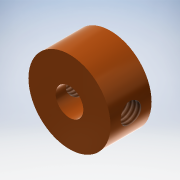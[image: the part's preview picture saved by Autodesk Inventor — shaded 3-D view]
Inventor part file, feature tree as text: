
AUTODESK INVENTOR PART (.ipt)
format: ipt  version: 2018.2 (Build 222227000, 227)  size: 127,488 bytes
history: native  units: mm
features: extrude x2, thread x2, sketch x2
ambient origin geometry x8: Origin, YZ Plane, XZ Plane, XY Plane, X Axis, Y Axis, Z Axis, Center Point
bodies: Solid1 (feature_tree)
feature tree (6):
  extrude  "Extrusion1"  Depth=8.0mm
  extrude  "Extrusion2"  Depth=2.0mm
  thread  "Thread2"  [1 undecoded]
  thread  "Thread3"  [1 undecoded]
  sketch  "Sketch1"  dims[d0=2.7mm d1=8.0mm]
  sketch  "Sketch2"  dims[d2=4.0mm d3=0.0mm d4=2.0mm d5=6.0mm d6=0.0mm d9=10.0mm d10=0.0mm d11=10.0mm d12=0.0mm]
note: 2 required parameter values undecoded (feature->parameter linkage not recoverable at this tier; creation-order binding heuristic only, values carry confidence <= 0.55)
